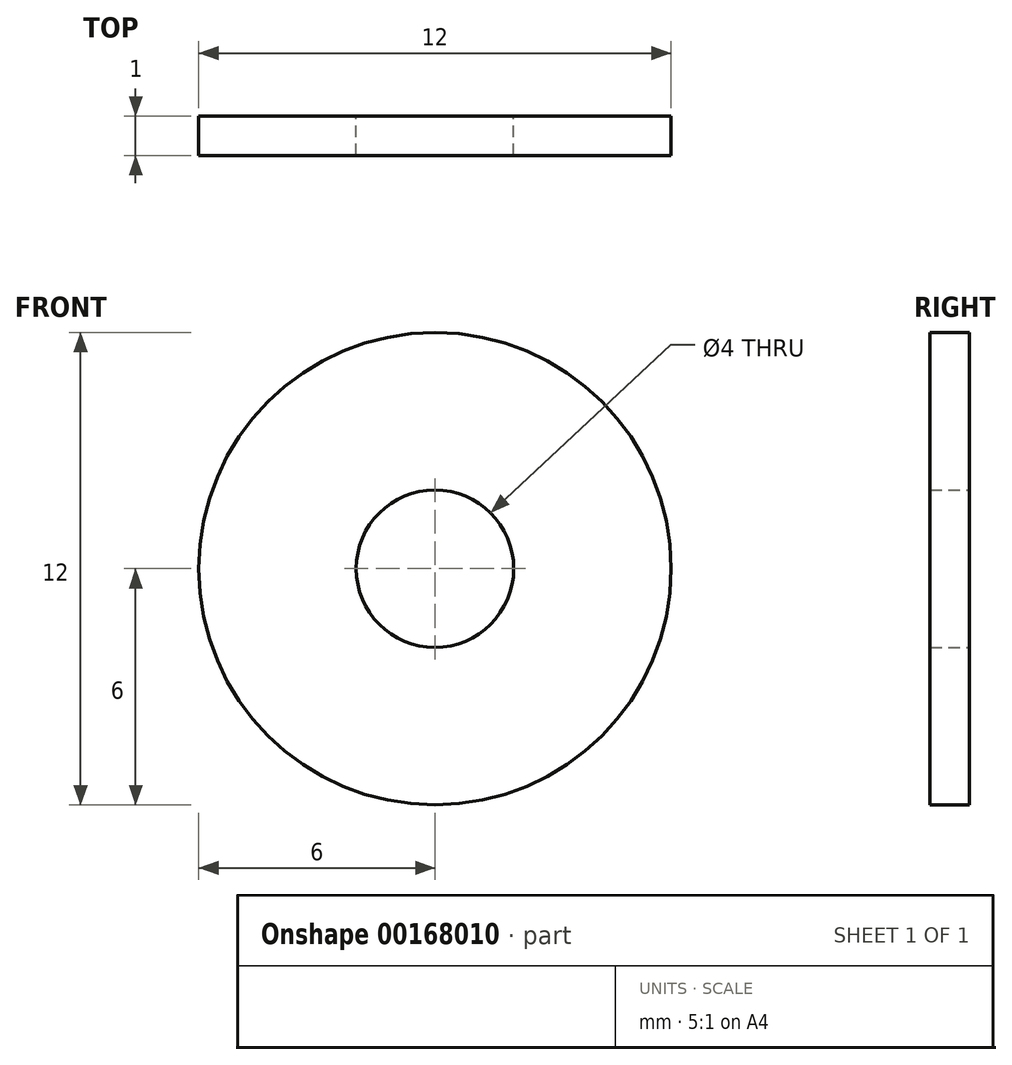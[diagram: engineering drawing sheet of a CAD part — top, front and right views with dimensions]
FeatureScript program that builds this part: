
annotation { "Feature Type Name" : "Feature", "Feature Type Description" : "" }
export const myFeature = defineFeature(function(context is Context, id is Id, definition is map)
    precondition{}
    {
        {
            var Q0;
            Q0=qCreatedBy(makeId("Front.planeOp"),FACE);
            var sketch = newSketch(context, id + "F0", { "sketchPlane" : qUnion([Q0])});
            skCircle(sketch, "E0", {"center": v(0, 0) * mm, "radius": 6 * mm});
            skCircle(sketch, "E1", {"center": v(0, 0) * mm, "radius": 2 * mm});
            skSolve(sketch);
        }
        {
            var Q0;
            Q0=makeQuery(id+"F0.imprint","IMPRINT",FACE,{"disambiguationData":[TD([[makeQuery(id+"F0.imprint","IMPRINT",EDGE,{"derivedFrom":sQuery(id+"F0.wireOp",EDGE,"E0")}),1.0]])]});
            extrude(context, id + "F1", {"entities" : qUnion([Q0]), "depth" : 1 * mm, "symmetric" : true});
        }
    });
